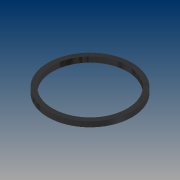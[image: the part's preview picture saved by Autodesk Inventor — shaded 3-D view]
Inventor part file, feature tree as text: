
AUTODESK INVENTOR PART (.ipt)
format: ipt  version: 2014 (Build 180170000, 170)  size: 77,824 bytes
history: native  units: mm
features: extrude x1, sketch x1
ambient origin geometry x8: Origin, YZ Plane, XZ Plane, XY Plane, X Axis, Y Axis, Z Axis, Center Point
bodies: Solid1 (feature_tree)
feature tree (2):
  extrude  "Extrusion1"  Depth=5.0mm
  sketch  "Sketch1"  dims[d0=80.0mm d1=71.0mm d2=5.0mm d3=0.0mm]
